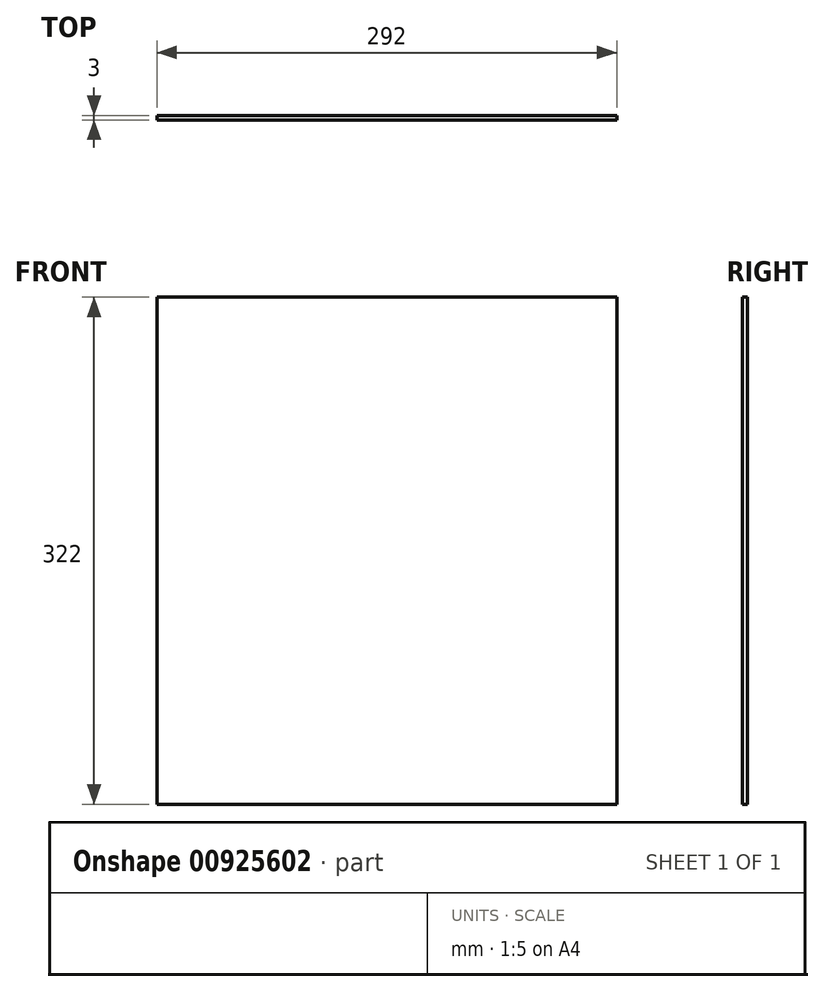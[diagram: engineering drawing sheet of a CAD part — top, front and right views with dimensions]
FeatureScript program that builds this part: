
annotation { "Feature Type Name" : "Feature", "Feature Type Description" : "" }
export const myFeature = defineFeature(function(context is Context, id is Id, definition is map)
    precondition{}
    {
        {
            var Q0;
            Q0=qCreatedBy(makeId("Front.planeOp"),FACE);
            var sketch = newSketch(context, id + "F0", { "sketchPlane" : qUnion([Q0])});
            skLineSegment(sketch, "E0.bottom", {"start": v(146, -161) * mm, "end": v(-146, -161) * mm});
            skLineSegment(sketch, "E0.top", {"start": v(146, 161) * mm, "end": v(-146, 161) * mm});
            skLineSegment(sketch, "E0.left", {"start": v(146, -161) * mm, "end": v(146, 161) * mm});
            skLineSegment(sketch, "E0.right", {"start": v(-146, -161) * mm, "end": v(-146, 161) * mm});
            skPoint(sketch, "E0.middle", {"position": v(0, 0) * mm});
            skSolve(sketch);
        }
        {
            var Q0;
            Q0 = qSketchRegion(id + "F0", true);
            extrude(context, id + "F1", {"entities" : qUnion([Q0]), "depth" : 3 * mm, "offsetDistance" : 25 * mm});
        }
    });
